# Revit family: KOMFORT EC D5B
name_source: partatom
category: Mechanical Equipment
units: mm (PartAtom-declared; Revit-internal decimal feet)

## family parameters
Always vertical = Yes
Classification = None
Cut with Voids When Loaded = No
Part Type = Normal
Room Calculation Point = No
Round Connector Dimension = Use Diameter
Shared = No
Work Plane-Based = No

## types (2) — shared parameters
00_20_Manufacturer = Blauberg
00_20_Name = Air hAndling unit
A = 500 mm  [stored 1.64042 ft]
Amperage = 1 A
Apparent Load = 163 VA
B = 600 mm
Casing Material = Polypropylene (black)
D = 150 mm  [stored 0.492126 ft]
Diameter = 150 mm  [stored 0.492126 ft]
Dy = 145 mm  [stored 0.475722 ft]
Filter = G4/G4, G7
H = 264 mm  [stored 0.866142 ft]
Height = 264 mm  [stored 0.866142 ft]
L = 900 mm  [stored 2.95276 ft]
Length = 900 mm  [stored 2.95276 ft]
Load Classification = HVAC
Maintenance zone material = <By Category>
Manufacturer = Blauberg
Maximum Air Flow = 220.0 m³/h
Number of Fase = 1
Power = 87 W
Sound pressure level at 3 m distance = 33 dBA
Temperature of moving air = -25…+40°С
URL = https://blaubergventilatoren.de
Voltage = 230 V
Weight = 14.00 kg
Width = 600 mm
h = -132 mm  [stored -0.433071 ft]
l = 50 mm  [stored 0.164042 ft]
l2 = 137 mm  [stored 0.449475 ft]
l22 = 144 mm
l222 = 137 mm  [stored 0.449475 ft]
l5 = 137 mm  [stored 0.449475 ft]
l6 = 137 mm  [stored 0.449475 ft]
zero-valued in all types: Default Elevation, h1

## per-type parameters (varying)
| type | E | l3 | l4 |
| KOMFORT EC D5B 180 S21 | Yes | 154 mm  [stored 0.505249 ft] | 154 mm  [stored 0.505249 ft] |
| KOMFORT EC D5B 180-E S21 | No | 132 mm  [stored 0.433071 ft] | 132 mm  [stored 0.433071 ft] |

note: column(s) folded — value = type name in every type: 00_20_Type

note: [stored X ft] marks values corroborated as IEEE doubles in the binary element streams (Revit-internal decimal feet)
